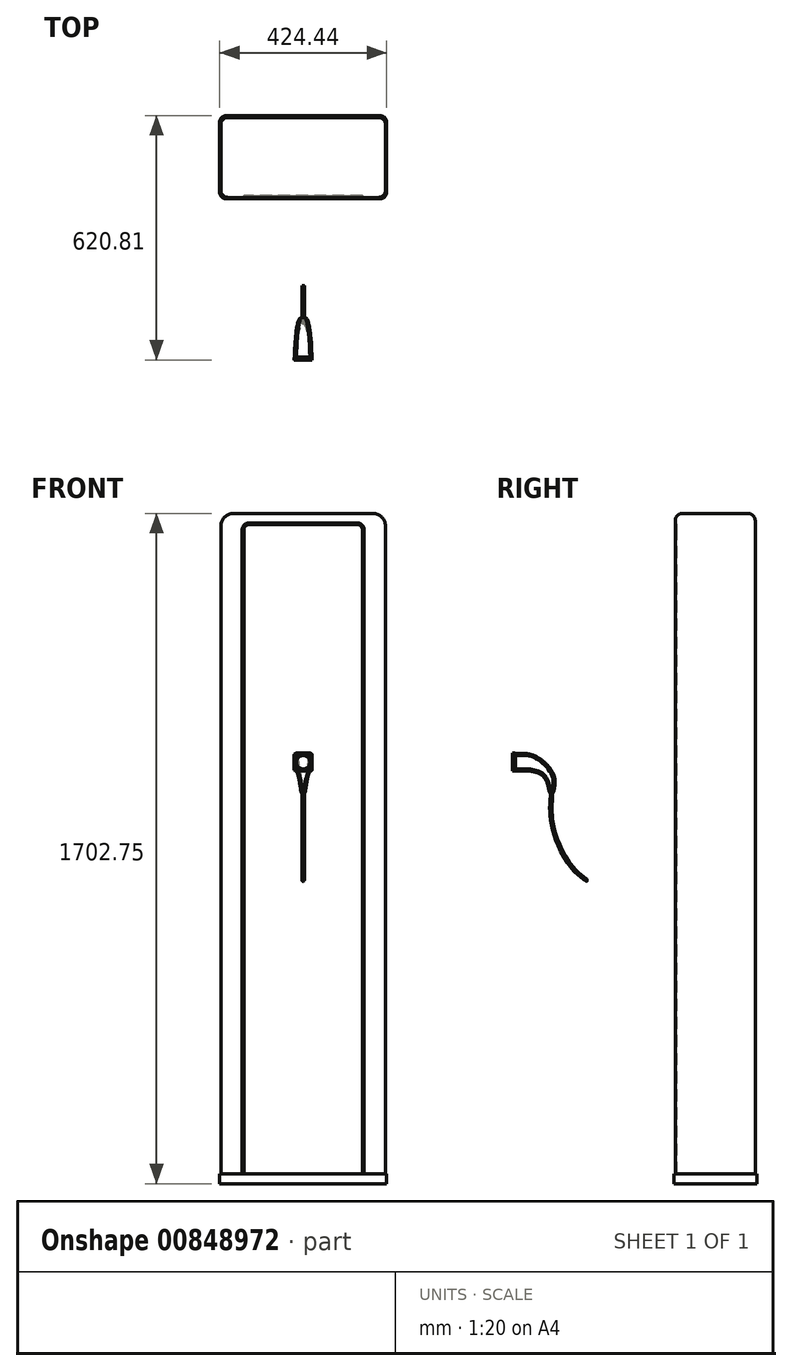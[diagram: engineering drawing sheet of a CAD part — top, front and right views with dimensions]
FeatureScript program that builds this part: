
annotation { "Feature Type Name" : "Feature", "Feature Type Description" : "" }
export const myFeature = defineFeature(function(context is Context, id is Id, definition is map)
    precondition{}
    {
        {
            var Q0;
            Q0=qCreatedBy(makeId("Right.planeOp"),FACE);
            var sketch = newSketch(context, id + "F0", { "sketchPlane" : qUnion([Q0])});
            skFitSpline(sketch, "E0", {"points": [v(0, -23.4) * mm, v(-9.12, 20.68) * mm, v(-41.42, 44.9) * mm, v(-91.55, 50.63) * mm], "startDerivative": vector(1.13, 133.95) * mm, "endDerivative": vector(-111.86, 1.62) * mm});
            skSolve(sketch);
        }
        {
            var Q0;
            Q0=qCreatedBy(makeId("Front.planeOp"),FACE);
            var sketch = newSketch(context, id + "F1", { "sketchPlane" : qUnion([Q0])});
            skLineSegment(sketch, "E1", {"start": v(-10.8, 21.4) * mm, "end": v(22.54, 21.4) * mm});
            skSolve(sketch);
        }
        {
            var Q0;
            Q0=qCreatedBy(makeId("Top.planeOp"),FACE);
            var Q1;
            Q1=sQuery(id+"F1.wireOp",EDGE,"E1");
            cPlane(context, id + "F2", {"entities" : qUnion([Q0, Q1]), "cplaneType" : CPlaneType.LINE_ANGLE, "offset" : 25.4 * mm, "angle" : 22.03 * degree, "width" : 152.4 * mm, "height" : 152.4 * mm});
        }
        {
            var Q0;
            Q0=qCreatedBy(makeId("Front.planeOp"),FACE);
            var Q1;
            Q1=sQuery(id+"F0.wireOp",VERTEX,"E0.2.internal");
            cPlane(context, id + "F3", {"entities" : qUnion([Q0, Q1]), "cplaneType" : CPlaneType.PLANE_POINT, "offset" : 25.4 * mm, "width" : 152.4 * mm, "height" : 152.4 * mm});
        }
        {
            var Q0;
            Q0=qCreatedBy(id+"F3.planeOp",FACE);
            var Q1;
            Q1=sQuery(id+"F0.wireOp",VERTEX,"E0.end");
            cPlane(context, id + "F4", {"entities" : qUnion([Q0, Q1]), "cplaneType" : CPlaneType.PLANE_POINT, "offset" : 25.4 * mm, "width" : 152.4 * mm, "height" : 152.4 * mm});
        }
        {
            var Q0;
            Q0=qCreatedBy(id+"F3.planeOp",FACE);
            var sketch = newSketch(context, id + "F5", { "sketchPlane" : qUnion([Q0])});
            skLineSegment(sketch, "E2", {"start": v(-5.8, 44.74) * mm, "end": v(10.1, 44.74) * mm});
            skSolve(sketch);
        }
        {
            var Q0;
            Q0=qCreatedBy(id+"F4.planeOp",FACE);
            var sketch = newSketch(context, id + "F6", { "sketchPlane" : qUnion([Q0])});
            skLineSegment(sketch, "E3", {"start": v(-6.81, 50.29) * mm, "end": v(13.62, 50.29) * mm});
            skSolve(sketch);
        }
        {
            var Q0;
            Q0=qCreatedBy(makeId("Top.planeOp"),FACE);
            var Q1;
            Q1=sQuery(id+"F5.wireOp",EDGE,"E2");
            cPlane(context, id + "F7", {"entities" : qUnion([Q0, Q1]), "cplaneType" : CPlaneType.LINE_ANGLE, "offset" : 25.4 * mm, "angle" : 70 * degree, "width" : 152.4 * mm, "height" : 152.4 * mm});
        }
        {
            var Q0;
            Q0=qCreatedBy(makeId("Top.planeOp"),FACE);
            var Q1;
            Q1=sQuery(id+"F6.wireOp",EDGE,"E3");
            cPlane(context, id + "F8", {"entities" : qUnion([Q0, Q1]), "cplaneType" : CPlaneType.LINE_ANGLE, "offset" : 25.4 * mm, "angle" : 90 * degree, "width" : 152.4 * mm, "height" : 152.4 * mm});
        }
        {
            var Q0;
            Q0=qCreatedBy(makeId("Top.planeOp"),FACE);
            var Q1;
            Q1=sQuery(id+"F0.wireOp",VERTEX,"E0.start");
            cPlane(context, id + "F9", {"entities" : qUnion([Q0, Q1]), "cplaneType" : CPlaneType.PLANE_POINT, "offset" : 25.4 * mm, "width" : 152.4 * mm, "height" : 152.4 * mm});
        }
        {
            var Q0;
            Q0=qCreatedBy(id+"F9.planeOp",FACE);
            var sketch = newSketch(context, id + "F10", { "sketchPlane" : qUnion([Q0])});
            skCircle(sketch, "E4", {"center": v(0, 0) * mm, "radius": 5.9 * mm});
            skSolve(sketch);
        }
        {
            var Q0;
            Q0=qCreatedBy(id+"F2.planeOp",FACE);
            var sketch = newSketch(context, id + "F11", { "sketchPlane" : qUnion([Q0])});
            skLineSegment(sketch, "E5.bottom", {"start": v(12.7, 13.11) * mm, "end": v(-12.7, 13.11) * mm});
            skLineSegment(sketch, "E5.top", {"start": v(12.7, -12.29) * mm, "end": v(-12.7, -12.29) * mm});
            skLineSegment(sketch, "E5.left", {"start": v(12.7, 13.11) * mm, "end": v(12.7, -12.29) * mm});
            skLineSegment(sketch, "E5.right", {"start": v(-12.7, 13.11) * mm, "end": v(-12.7, -12.29) * mm});
            skPoint(sketch, "E5.middle", {"position": v(0, 0.41) * mm});
            skSolve(sketch);
        }
        {
            var Q0;
            Q0=qCreatedBy(id+"F7.planeOp",FACE);
            var sketch = newSketch(context, id + "F12", { "sketchPlane" : qUnion([Q0])});
            skLineSegment(sketch, "E6.bottom", {"start": v(-19.05, 8.99) * mm, "end": v(19.05, 8.99) * mm});
            skLineSegment(sketch, "E6.top", {"start": v(-19.05, 47.09) * mm, "end": v(19.05, 47.09) * mm});
            skLineSegment(sketch, "E6.left", {"start": v(-19.05, 8.99) * mm, "end": v(-19.05, 47.09) * mm});
            skLineSegment(sketch, "E6.right", {"start": v(19.05, 8.99) * mm, "end": v(19.05, 47.09) * mm});
            skPoint(sketch, "E6.middle", {"position": v(0, 28.04) * mm});
            skSolve(sketch);
        }
        {
            var Q0;
            Q0=qCreatedBy(id+"F8.planeOp",FACE);
            var sketch = newSketch(context, id + "F13", { "sketchPlane" : qUnion([Q0])});
            skLineSegment(sketch, "E7.bottom", {"start": v(-22.22, 28.4) * mm, "end": v(22.23, 28.4) * mm});
            skLineSegment(sketch, "E7.top", {"start": v(-22.23, 72.85) * mm, "end": v(22.22, 72.85) * mm});
            skLineSegment(sketch, "E7.left", {"start": v(-22.22, 28.4) * mm, "end": v(-22.23, 72.85) * mm});
            skLineSegment(sketch, "E7.right", {"start": v(22.23, 28.4) * mm, "end": v(22.22, 72.85) * mm});
            skPoint(sketch, "E7.middle", {"position": v(0, 50.63) * mm});
            skSolve(sketch);
        }
        {
            var Q0;
            Q0=makeQuery(id+"F13.imprint","IMPRINT",FACE,{"disambiguationData":[TD([[makeQuery(id+"F13.imprint","IMPRINT",EDGE,{"derivedFrom":sQuery(id+"F13.wireOp",EDGE,"E7.bottom")}),1.0]])]});
            var Q1;
            Q1=makeQuery(id+"F12.imprint","IMPRINT",FACE,{"disambiguationData":[TD([[makeQuery(id+"F12.imprint","IMPRINT",EDGE,{"derivedFrom":sQuery(id+"F12.wireOp",EDGE,"E6.bottom")}),1.0]])]});
            var Q2;
            Q2=makeQuery(id+"F11.imprint","IMPRINT",FACE,{"disambiguationData":[TD([[makeQuery(id+"F11.imprint","IMPRINT",EDGE,{"derivedFrom":sQuery(id+"F11.wireOp",EDGE,"E5.bottom")}),1.0]])]});
            var Q3;
            Q3=makeQuery(id+"F10.imprint","IMPRINT",FACE,{"disambiguationData":[TD([[makeQuery(id+"F10.imprint","IMPRINT",EDGE,{"derivedFrom":sQuery(id+"F10.wireOp",EDGE,"E4")}),1.0]])]});
            loft(context, id + "F14", {"sheetProfilesArray" : [{ "sheetProfileEntities" : qUnion([Q0]) }, { "sheetProfileEntities" : qUnion([Q1]) }, { "sheetProfileEntities" : qUnion([Q2]) }, { "sheetProfileEntities" : qUnion([Q3]) }]});
        }
        {
            var Q0;
            Q0=makeQuery(id+"F14.opLoft","SWEPT_EDGE",EDGE,{"disambiguationData":[OSD([sQuery(id+"F10.wireOp",EDGE,"E4"),sQuery(id+"F11.wireOp",EDGE,"E5.top"),sQuery(id+"F11.wireOp",EDGE,"E5.left"),sQuery(id+"F12.wireOp",EDGE,"E6.top"),sQuery(id+"F12.wireOp",EDGE,"E6.left"),sQuery(id+"F13.wireOp",EDGE,"E7.top"),sQuery(id+"F13.wireOp",EDGE,"E7.left"),sQuery(id+"F13.wireOp",EDGE,"E7.right")])]});
            var Q1;
            Q1=makeQuery(id+"F14.opLoft","SWEPT_EDGE",EDGE,{"disambiguationData":[OSD([sQuery(id+"F11.wireOp",EDGE,"E5.bottom"),sQuery(id+"F11.wireOp",EDGE,"E5.left"),sQuery(id+"F12.wireOp",EDGE,"E6.bottom"),sQuery(id+"F12.wireOp",EDGE,"E6.left"),sQuery(id+"F13.wireOp",EDGE,"E7.bottom"),sQuery(id+"F13.wireOp",EDGE,"E7.left")])]});
            var Q2;
            Q2=makeQuery(id+"F14.opLoft","SWEPT_EDGE",EDGE,{"disambiguationData":[OSD([sQuery(id+"F10.wireOp",EDGE,"E4"),sQuery(id+"F11.wireOp",EDGE,"E5.top"),sQuery(id+"F11.wireOp",EDGE,"E5.right"),sQuery(id+"F12.wireOp",EDGE,"E6.top"),sQuery(id+"F12.wireOp",EDGE,"E6.right"),sQuery(id+"F13.wireOp",EDGE,"E7.bottom"),sQuery(id+"F13.wireOp",EDGE,"E7.top"),sQuery(id+"F13.wireOp",EDGE,"E7.right")])]});
            var Q3;
            Q3=makeQuery(id+"F14.opLoft","SWEPT_EDGE",EDGE,{"disambiguationData":[OSD([sQuery(id+"F10.wireOp",EDGE,"E4"),sQuery(id+"F11.wireOp",EDGE,"E5.bottom"),sQuery(id+"F11.wireOp",EDGE,"E5.right"),sQuery(id+"F12.wireOp",EDGE,"E6.bottom"),sQuery(id+"F12.wireOp",EDGE,"E6.right"),sQuery(id+"F13.wireOp",EDGE,"E7.bottom"),sQuery(id+"F13.wireOp",EDGE,"E7.left"),sQuery(id+"F13.wireOp",EDGE,"E7.right")])]});
            fillet(context, id + "F15", {"entities" : qUnion([Q0, Q1, Q2, Q3]), "radius" : 5.08 * mm, "tangentPropagation" : true, "allowEdgeOverflow" : false});
        }
        {
            var Q0;
            Q0=qCreatedBy(id+"F4.planeOp",FACE);
            cPlane(context, id + "F16", {"entities" : qUnion([Q0]), "cplaneType" : CPlaneType.OFFSET, "offset" : 0.64 * mm, "width" : 152.4 * mm, "height" : 152.4 * mm});
        }
        {
            var Q0;
            Q0=qCreatedBy(id+"F16.planeOp",FACE);
            var sketch = newSketch(context, id + "F17", { "sketchPlane" : qUnion([Q0])});
            skLineSegment(sketch, "E8.bottom", {"start": v(-22.86, 73.49) * mm, "end": v(22.86, 73.49) * mm});
            skLineSegment(sketch, "E8.top", {"start": v(-22.86, 27.77) * mm, "end": v(22.86, 27.77) * mm});
            skLineSegment(sketch, "E8.left", {"start": v(-22.86, 73.49) * mm, "end": v(-22.86, 27.77) * mm});
            skLineSegment(sketch, "E8.right", {"start": v(22.86, 73.49) * mm, "end": v(22.86, 27.77) * mm});
            skPoint(sketch, "E8.middle", {"position": v(0, 50.63) * mm});
            skSolve(sketch);
        }
        {
            var Q0;
            Q0=makeQuery(id+"F17.imprint","IMPRINT",FACE,{"disambiguationData":[TD([[makeQuery(id+"F17.imprint","IMPRINT",EDGE,{"derivedFrom":sQuery(id+"F17.wireOp",EDGE,"E8.bottom")}),-1.0]])]});
            extrude(context, id + "F18", {"entities" : qUnion([Q0]), "depth" : 6.35 * mm, "offsetDistance" : 25.4 * mm});
        }
        {
            var Q0;
            Q0=makeQuery(id+"F18.opExtrude","SWEPT_EDGE",EDGE,{"disambiguationData":[OSD([sQuery(id+"F17.wireOp",EDGE,"E8.bottom"),sQuery(id+"F17.wireOp",EDGE,"E8.right")])]});
            var Q1;
            Q1=makeQuery(id+"F18.opExtrude","SWEPT_EDGE",EDGE,{"disambiguationData":[OSD([sQuery(id+"F17.wireOp",EDGE,"E8.top"),sQuery(id+"F17.wireOp",EDGE,"E8.right")])]});
            var Q2;
            Q2=makeQuery(id+"F18.opExtrude","SWEPT_EDGE",EDGE,{"disambiguationData":[OSD([sQuery(id+"F17.wireOp",EDGE,"E8.top"),sQuery(id+"F17.wireOp",EDGE,"E8.left")])]});
            var Q3;
            Q3=makeQuery(id+"F18.opExtrude","SWEPT_EDGE",EDGE,{"disambiguationData":[OSD([sQuery(id+"F17.wireOp",EDGE,"E8.bottom"),sQuery(id+"F17.wireOp",EDGE,"E8.left")])]});
            fillet(context, id + "F19", {"entities" : qUnion([Q0, Q1, Q2, Q3]), "radius" : 5.08 * mm, "tangentPropagation" : true, "allowEdgeOverflow" : false});
        }
        {
            var Q0;
            {var subQ0=sQuery(id+"F13.wireOp",EDGE,"E7.top");var subQ1=sQuery(id+"F13.wireOp",EDGE,"E7.left");var subQ2=sQuery(id+"F13.wireOp",EDGE,"E7.right");Q0=makeQuery(id+"F15.opFillet","BLEND_EDGE",EDGE,{"blendedFrom":[makeQuery(id+"F14.opLoft","SWEPT_EDGE",EDGE,{"disambiguationData":[OSD([sQuery(id+"F10.wireOp",EDGE,"E4"),sQuery(id+"F11.wireOp",EDGE,"E5.top"),sQuery(id+"F11.wireOp",EDGE,"E5.left"),sQuery(id+"F12.wireOp",EDGE,"E6.top"),sQuery(id+"F12.wireOp",EDGE,"E6.left"),subQ0,subQ1,subQ2])]}),makeQuery(id+"F14.opLoft","CAP_FACE",FACE,{"disambiguationData":[OSD([makeQuery(id+"F13.imprint","IMPRINT",FACE,{"disambiguationData":[TD([[makeQuery(id+"F13.imprint","IMPRINT",EDGE,{"derivedFrom":sQuery(id+"F13.wireOp",EDGE,"E7.bottom")}),1.0]])]})])],"isStart":true})],"blendedInto":[makeQuery(id+"F14.opLoft","CAP_FACE",FACE,{"disambiguationData":[OSD([makeQuery(id+"F13.imprint","IMPRINT",FACE,{"disambiguationData":[TD([[makeQuery(id+"F13.imprint","IMPRINT",EDGE,{"derivedFrom":sQuery(id+"F13.wireOp",EDGE,"E7.bottom")}),1.0]])]})])],"isStart":true})]});}
            var Q1;
            Q1=makeQuery(id+"F14.opLoft","MID_CAP_EDGE",EDGE,{"disambiguationData":[OSD([sQuery(id+"F13.wireOp",EDGE,"E7.bottom"),sQuery(id+"F13.wireOp",EDGE,"E7.top"),sQuery(id+"F13.wireOp",EDGE,"E7.left")])],"capPos":0.0});
            var Q2;
            Q2=makeQuery(id+"F18.opExtrude","CAP_EDGE",EDGE,{"disambiguationData":[OSD([sQuery(id+"F17.wireOp",EDGE,"E8.bottom")])],"isStart":true});
            var Q3;
            {var subQ0=sQuery(id+"F17.wireOp",EDGE,"E8.right");var subQ1=sQuery(id+"F17.wireOp",EDGE,"E8.bottom");Q3=makeQuery(id+"F19.opFillet","BLEND_EDGE",EDGE,{"blendedFrom":[makeQuery(id+"F18.opExtrude","SWEPT_EDGE",EDGE,{"disambiguationData":[OSD([subQ1,subQ0])]}),makeQuery(id+"F18.opExtrude","CAP_FACE",FACE,{"disambiguationData":[OSD([subQ1,sQuery(id+"F17.wireOp",EDGE,"E8.top"),sQuery(id+"F17.wireOp",EDGE,"E8.left"),subQ0])],"isStart":true})],"blendedInto":[makeQuery(id+"F18.opExtrude","CAP_FACE",FACE,{"disambiguationData":[OSD([subQ1,sQuery(id+"F17.wireOp",EDGE,"E8.top"),sQuery(id+"F17.wireOp",EDGE,"E8.left"),subQ0])],"isStart":true})]});}
            fillet(context, id + "F20", {"entities" : qUnion([Q0, Q1, Q2, Q3]), "radius" : 0.64 * mm, "tangentPropagation" : true, "allowEdgeOverflow" : false});
        }
        {
            var Q0;
            Q0=qCreatedBy(id+"F9.planeOp",FACE);
            cPlane(context, id + "F21", {"entities" : qUnion([Q0]), "cplaneType" : CPlaneType.OFFSET, "offset" : 4.06 * mm, "oppositeDirection" : true, "width" : 152.4 * mm, "height" : 152.4 * mm});
        }
        {
            var Q0;
            Q0=qCreatedBy(id+"F21.planeOp",FACE);
            var sketch = newSketch(context, id + "F22", { "sketchPlane" : qUnion([Q0])});
            skCircle(sketch, "E9", {"center": v(0, 0) * mm, "radius": 3.89 * mm});
            skSolve(sketch);
        }
        {
            var Q1;
            Q1 = qSketchRegion(id + "F10", true);
            var Q2;
            Q2=makeQuery(id+"F22.imprint","IMPRINT",FACE,{"disambiguationData":[TD([[makeQuery(id+"F22.imprint","IMPRINT",EDGE,{"derivedFrom":sQuery(id+"F22.wireOp",EDGE,"E9")}),1.0]])]});
            loft(context, id + "F23", {"sheetProfilesArray" : [{ "sheetProfileEntities" : qUnion([Q1]) }, { "sheetProfileEntities" : qUnion([Q2]) }]});
        }
        {
            var Q0;
            Q0=qCreatedBy(id+"F16.planeOp",FACE);
            var sketch = newSketch(context, id + "F24", { "sketchPlane" : qUnion([Q0])});
            skCircle(sketch, "E10", {"center": v(0, 50.7) * mm, "radius": 18.5 * mm});
            skCircle(sketch, "E11", {"center": v(0, 50.7) * mm, "radius": 17.03 * mm});
            skSolve(sketch);
        }
        {
            var Q0;
            Q0 = qSketchRegion(id + "F24", true);
            extrude(context, id + "F25", {"entities" : qUnion([Q0]), "operationType" : NewBodyOperationType.REMOVE, "depth" : 25.4 * mm, "offsetDistance" : 25.4 * mm});
        }
        {
            var Q0;
            {var subQ0=sQuery(id+"F17.wireOp",EDGE,"E8.left");var subQ1=sQuery(id+"F17.wireOp",EDGE,"E8.bottom");var subQ2=sQuery(id+"F17.wireOp",EDGE,"E8.top");var subQ3=sQuery(id+"F17.wireOp",EDGE,"E8.right");Q0=makeQuery(id+"F25.boolean.opBoolean","SPLIT",FACE,{"disambiguationData":[TD([makeQuery(id+"F18.opExtrude","SWEPT_FACE",FACE,{"disambiguationData":[OSD([subQ1])]})])],"derivedFrom":makeQuery(id+"F18.opExtrude","CAP_FACE",FACE,{"disambiguationData":[OSD([subQ1,subQ2,subQ0,subQ3])],"isStart":false})});}
            shell(context, id + "F26", {"entities" : qUnion([Q0]), "thickness" : 1.27 * mm});
        }
        {
            var Q0;
            Q0=qCreatedBy(makeId("Right.planeOp"),FACE);
            var sketch = newSketch(context, id + "F27", { "sketchPlane" : qUnion([Q0])});
            skFitSpline(sketch, "E12", {"points": [v(0, -27.5) * mm, v(0, -95.02) * mm, v(70.79, -235.24) * mm, v(177.5, -258.95) * mm, v(256.82, -180.23) * mm, v(319.02, -94.16) * mm], "startDerivative": vector(8.07, -227.5) * mm, "endDerivative": vector(587.7, 102.39) * mm});
            skSolve(sketch);
        }
        {
            var Q0;
            Q0=qCreatedBy(id+"F9.planeOp",FACE);
            var sketch = newSketch(context, id + "F28", { "sketchPlane" : qUnion([Q0])});
            skCircle(sketch, "E13", {"center": v(0, 0) * mm, "radius": 2.9 * mm});
            skSolve(sketch);
        }
        {
            var Q0;
            Q0 = qSketchRegion(id + "F28", true);
            var Q1;
            Q1=sQuery(id+"F27.wireOp",EDGE,"E12");
            sweep(context, id + "F29", {"profiles" : qUnion([Q0]), "path" : qUnion([Q1])});
        }
        {
            var Q0;
            Q0=makeQuery(id+"F23.opLoft","SWEPT_FACE",FACE,{"disambiguationData":[OSD([sQuery(id+"F10.wireOp",EDGE,"E4"),sQuery(id+"F22.wireOp",EDGE,"E9")])]});
            fillet(context, id + "F30", {"entities" : qUnion([Q0]), "radius" : 0.64 * mm, "tangentPropagation" : true, "allowEdgeOverflow" : false});
        }
        {
            var Q0;
            Q0=qCreatedBy(makeId("Front.planeOp"),FACE);
            var Q1;
            Q1=sQuery(id+"F27.wireOp",VERTEX,"E12.end");
            cPlane(context, id + "F31", {"entities" : qUnion([Q0, Q1]), "cplaneType" : CPlaneType.PLANE_POINT, "offset" : 25.4 * mm, "width" : 152.4 * mm, "height" : 152.4 * mm});
        }
        {
            var Q0;
            Q0=qCreatedBy(id+"F31.planeOp",FACE);
            var sketch = newSketch(context, id + "F32", { "sketchPlane" : qUnion([Q0])});
            skLineSegment(sketch, "E14.bottom", {"start": v(137.8, 653.7) * mm, "end": v(-137.8, 653.7) * mm});
            skLineSegment(sketch, "E14.top", {"start": v(149.86, -994.76) * mm, "end": v(-149.86, -994.76) * mm});
            skLineSegment(sketch, "E14.left", {"start": v(149.86, 641.64) * mm, "end": v(149.86, -994.76) * mm});
            skLineSegment(sketch, "E14.right", {"start": v(-149.86, 641.64) * mm, "end": v(-149.86, -994.76) * mm});
            skPoint(sketch, "E14.middle", {"position": v(0, -170.53) * mm});
            skPoint(sketch, "E15.visualSharp", {"position": v(-149.86, 653.7) * mm});
            skArc(sketch, "E15.filletArc", {"start": v(-137.8, 653.7) * mm, "mid": v(-146.33, 650.17) * mm, "end": v(-149.86, 641.64) * mm});
            skPoint(sketch, "E16.visualSharp", {"position": v(149.86, 653.7) * mm});
            skArc(sketch, "E16.filletArc", {"start": v(149.86, 641.64) * mm, "mid": v(146.33, 650.17) * mm, "end": v(137.8, 653.7) * mm});
            skSolve(sketch);
        }
        {
            var Q0;
            Q0=qCreatedBy(id+"F31.planeOp",FACE);
            cPlane(context, id + "F33", {"entities" : qUnion([Q0]), "cplaneType" : CPlaneType.OFFSET, "offset" : 4.57 * mm, "width" : 152.4 * mm, "height" : 152.4 * mm});
        }
        {
            var Q0;
            Q0=qCreatedBy(id+"F33.planeOp",FACE);
            var sketch = newSketch(context, id + "F34", { "sketchPlane" : qUnion([Q0])});
            skLineSegment(sketch, "E17.bottom", {"start": v(-177.44, 682.59) * mm, "end": v(177.44, 682.59) * mm});
            skLineSegment(sketch, "E17.left", {"start": v(-209.19, 650.84) * mm, "end": v(-209.19, -994.76) * mm});
            skLineSegment(sketch, "E17.right", {"start": v(209.19, 650.84) * mm, "end": v(209.19, -994.76) * mm});
            skPoint(sketch, "E17.middle", {"position": v(0, -156.09) * mm});
            skPoint(sketch, "E18.visualSharp", {"position": v(-209.19, 682.59) * mm});
            skArc(sketch, "E18.filletArc", {"start": v(-177.44, 682.59) * mm, "mid": v(-199.89, 673.29) * mm, "end": v(-209.19, 650.84) * mm});
            skPoint(sketch, "E19.visualSharp", {"position": v(209.19, 682.59) * mm});
            skArc(sketch, "E19.filletArc", {"start": v(209.19, 650.84) * mm, "mid": v(199.89, 673.29) * mm, "end": v(177.44, 682.59) * mm});
            skLineSegment(sketch, "E20", {"start": v(-209.19, -994.76) * mm, "end": v(209.19, -994.76) * mm});
            skSolve(sketch);
        }
        {
            var Q0;
            Q0=makeQuery(id+"F34.imprint","IMPRINT",FACE,{"disambiguationData":[TD([[makeQuery(id+"F34.imprint","IMPRINT",EDGE,{"derivedFrom":sQuery(id+"F34.wireOp",EDGE,"E17.bottom")}),-1.0]])]});
            extrude(context, id + "F35", {"entities" : qUnion([Q0]), "oppositeDirection" : true, "depth" : 203.2 * mm, "offsetDistance" : 25.4 * mm});
        }
        {
            var Q0;
            Q0 = qSketchRegion(id + "F32", true);
            extrude(context, id + "F36", {"entities" : qUnion([Q0]), "operationType" : NewBodyOperationType.REMOVE, "depth" : 228.6 * mm, "offsetDistance" : 25.4 * mm});
        }
        {
            var Q0;
            Q0=makeQuery(id+"F36.boolean.opBoolean","INTERSECT",EDGE,{"derivedFrom":[makeQuery(id+"F35.opExtrude","CAP_FACE",FACE,{"disambiguationData":[OSD([sQuery(id+"F34.wireOp",EDGE,"E17.bottom"),sQuery(id+"F34.wireOp",EDGE,"E17.left"),sQuery(id+"F34.wireOp",EDGE,"E17.right"),sQuery(id+"F34.wireOp",EDGE,"E18.filletArc"),sQuery(id+"F34.wireOp",EDGE,"E19.filletArc"),sQuery(id+"F34.wireOp",EDGE,"E20")])],"isStart":true}),makeQuery(id+"F36.opExtrude","SWEPT_FACE",FACE,{"disambiguationData":[OSD([sQuery(id+"F32.wireOp",EDGE,"E14.bottom")])]})]});
            chamfer(context, id + "F37", {"entities" : qUnion([Q0]), "width" : 5.08 * mm, "tangentPropagation" : true});
        }
        {
            var Q0;
            Q0=makeQuery(id+"F35.opExtrude","CAP_EDGE",EDGE,{"disambiguationData":[OSD([sQuery(id+"F34.wireOp",EDGE,"E18.filletArc")])],"isStart":true});
            var Q1;
            Q1=makeQuery(id+"F35.opExtrude","CAP_EDGE",EDGE,{"disambiguationData":[OSD([sQuery(id+"F34.wireOp",EDGE,"E17.bottom")])],"isStart":false});
            fillet(context, id + "F38", {"entities" : qUnion([Q0, Q1]), "radius" : 17.78 * mm, "tangentPropagation" : true, "allowEdgeOverflow" : false});
        }
        {
            var Q0;
            Q0=qCreatedBy(makeId("Top.planeOp"),FACE);
            var Q1;
            Q1=sQuery(id+"F34.wireOp",VERTEX,"E17.right.end");
            cPlane(context, id + "F39", {"entities" : qUnion([Q0, Q1]), "cplaneType" : CPlaneType.PLANE_POINT, "offset" : 25.4 * mm, "width" : 152.4 * mm, "height" : 152.4 * mm});
        }
        {
            var Q0;
            Q0=qCreatedBy(id+"F39.planeOp",FACE);
            var sketch = newSketch(context, id + "F40", { "sketchPlane" : qUnion([Q0])});
            skLineSegment(sketch, "E21.bottom", {"start": v(-195.71, 311.1) * mm, "end": v(195.71, 311.1) * mm});
            skLineSegment(sketch, "E21.top", {"start": v(-195.71, 522.28) * mm, "end": v(195.71, 522.28) * mm});
            skLineSegment(sketch, "E21.left", {"start": v(-212.22, 327.61) * mm, "end": v(-212.22, 505.77) * mm});
            skLineSegment(sketch, "E21.right", {"start": v(212.22, 327.61) * mm, "end": v(212.22, 505.77) * mm});
            skPoint(sketch, "E21.middle", {"position": v(0, 416.7) * mm});
            skPoint(sketch, "E22.visualSharp", {"position": v(-212.22, 311.1) * mm});
            skArc(sketch, "E22.filletArc", {"start": v(-212.22, 327.61) * mm, "mid": v(-207.39, 315.94) * mm, "end": v(-195.71, 311.1) * mm});
            skPoint(sketch, "E23.visualSharp", {"position": v(212.22, 311.1) * mm});
            skArc(sketch, "E23.filletArc", {"start": v(195.71, 311.1) * mm, "mid": v(207.39, 315.94) * mm, "end": v(212.22, 327.61) * mm});
            skPoint(sketch, "E24.visualSharp", {"position": v(212.22, 522.28) * mm});
            skArc(sketch, "E24.filletArc", {"start": v(212.22, 505.77) * mm, "mid": v(207.39, 517.44) * mm, "end": v(195.71, 522.28) * mm});
            skPoint(sketch, "E25.visualSharp", {"position": v(-212.22, 522.28) * mm});
            skArc(sketch, "E25.filletArc", {"start": v(-195.71, 522.28) * mm, "mid": v(-207.39, 517.44) * mm, "end": v(-212.22, 505.77) * mm});
            skSolve(sketch);
        }
        {
            var Q0;
            Q0 = qSketchRegion(id + "F40", true);
            extrude(context, id + "F41", {"entities" : qUnion([Q0]), "oppositeDirection" : true, "depth" : 25.4 * mm, "offsetDistance" : 25.4 * mm});
        }
    });
